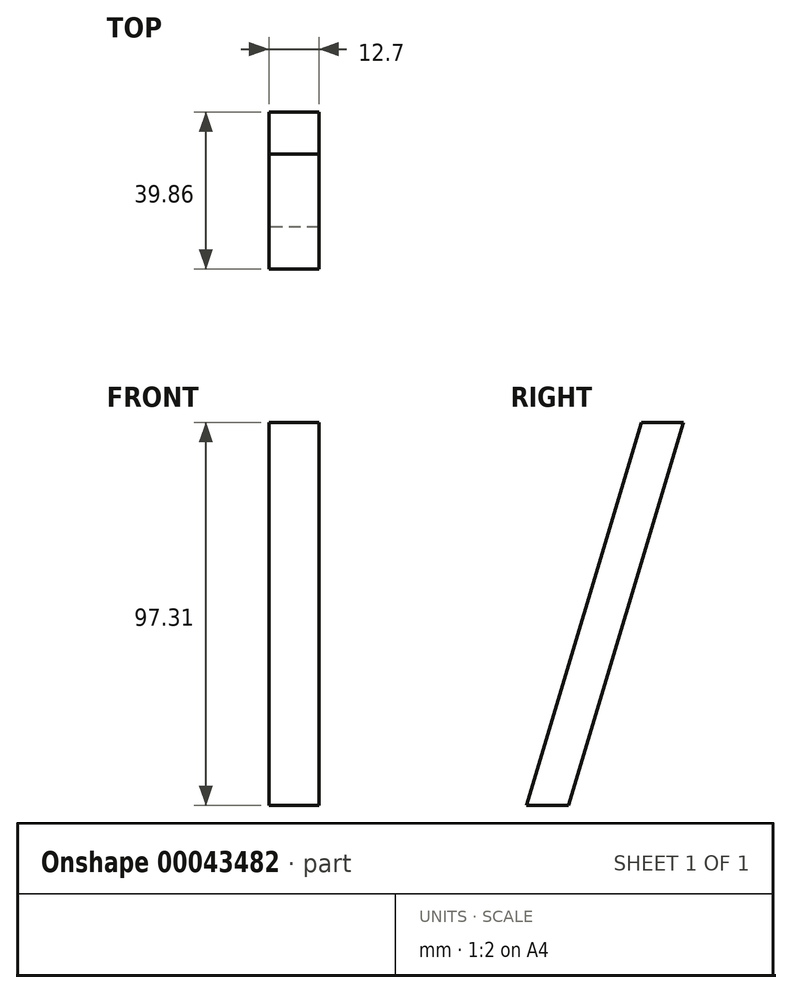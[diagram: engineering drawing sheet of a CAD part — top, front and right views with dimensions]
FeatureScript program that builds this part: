
annotation { "Feature Type Name" : "Feature", "Feature Type Description" : "" }
export const myFeature = defineFeature(function(context is Context, id is Id, definition is map)
    precondition{}
    {
        {
            var Q0;
            Q0=qCreatedBy(makeId("Right.planeOp"),FACE);
            var sketch = newSketch(context, id + "F0", { "sketchPlane" : qUnion([Q0])});
            skLineSegment(sketch, "E0", {"start": v(-10.32, 46.49) * mm, "end": v(0.32, 46.49) * mm});
            skLineSegment(sketch, "E1", {"start": v(0.32, 46.49) * mm, "end": v(-28.9, -50.82) * mm});
            skLineSegment(sketch, "E2", {"start": v(-28.9, -50.82) * mm, "end": v(-39.54, -50.82) * mm});
            skLineSegment(sketch, "E3", {"start": v(-39.54, -50.82) * mm, "end": v(-10.32, 46.49) * mm});
            skSolve(sketch);
        }
        {
            var Q0;
            Q0 = qSketchRegion(id + "F0", true);
            extrude(context, id + "F1", {"entities" : qUnion([Q0]), "depth" : 12.7 * mm});
        }
    });
